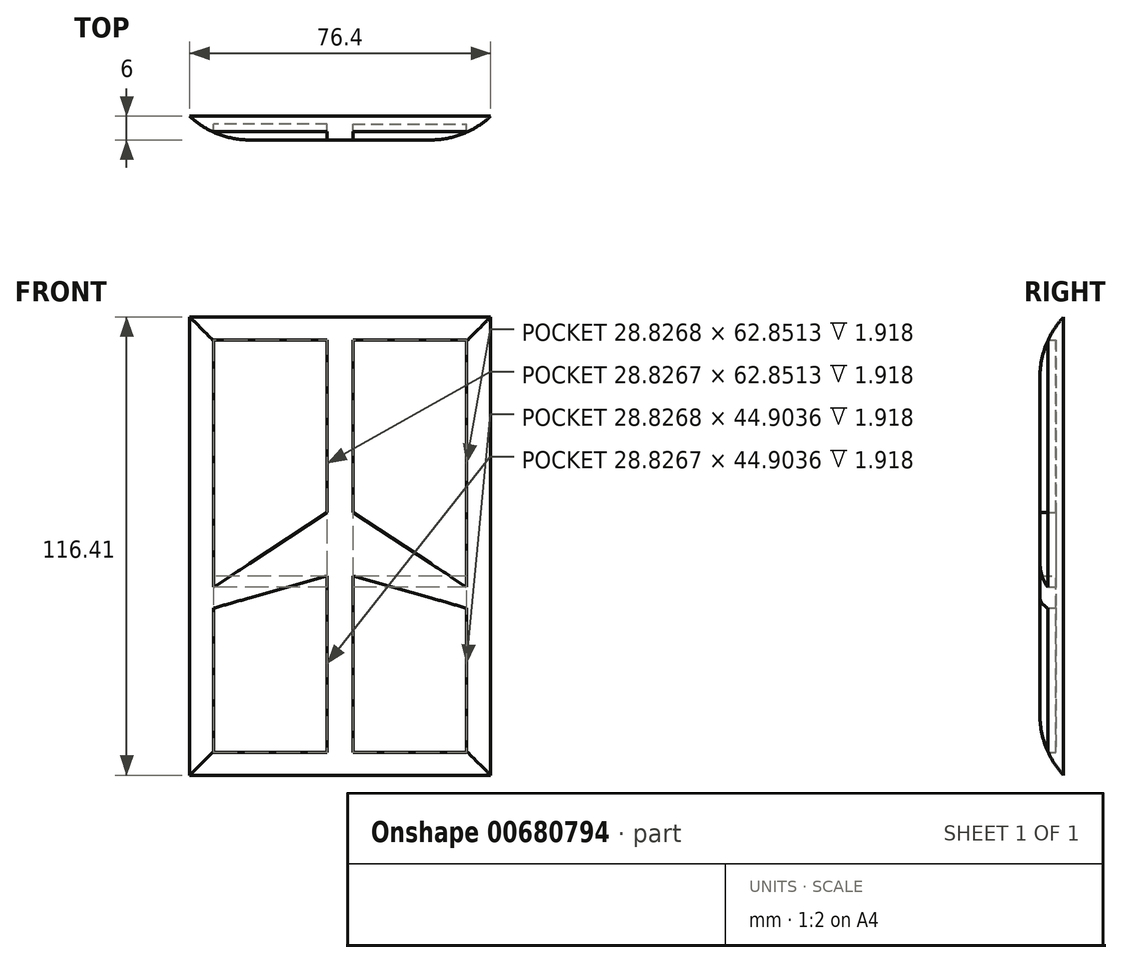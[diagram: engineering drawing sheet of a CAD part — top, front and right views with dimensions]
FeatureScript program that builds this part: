
annotation { "Feature Type Name" : "Feature", "Feature Type Description" : "" }
export const myFeature = defineFeature(function(context is Context, id is Id, definition is map)
    precondition{}
    {
        {
            var Q0;
            Q0=qCreatedBy(makeId("Front.planeOp"),FACE);
            var sketch = newSketch(context, id + "F0", { "sketchPlane" : qUnion([Q0])});
            skLineSegment(sketch, "E0.bottom", {"start": v(-19.82, 37.7) * mm, "end": v(44.44, 37.7) * mm});
            skLineSegment(sketch, "E0.top", {"start": v(-19.82, -67.16) * mm, "end": v(44.44, -67.16) * mm});
            skLineSegment(sketch, "E0.left", {"start": v(-19.82, 37.7) * mm, "end": v(-19.82, -67.16) * mm});
            skLineSegment(sketch, "E0.right", {"start": v(44.44, 37.7) * mm, "end": v(44.44, -67.16) * mm});
            skPoint(sketch, "E1", {"position": v(-25.9, -72.94) * mm});
            skPoint(sketch, "E2", {"position": v(50.51, -72.94) * mm});
            skPoint(sketch, "E3", {"position": v(50.51, 43.47) * mm});
            skPoint(sketch, "E4", {"position": v(-25.9, 43.47) * mm});
            skLineSegment(sketch, "E5", {"start": v(-25.9, -72.94) * mm, "end": v(50.51, -72.94) * mm});
            skLineSegment(sketch, "E6", {"start": v(-25.9, 43.47) * mm, "end": v(50.51, 43.47) * mm});
            skLineSegment(sketch, "E7", {"start": v(50.51, -72.94) * mm, "end": v(50.51, 43.47) * mm});
            skLineSegment(sketch, "E8", {"start": v(-25.9, -72.94) * mm, "end": v(-25.9, 43.47) * mm});
            skPoint(sketch, "E9", {"position": v(12.31, -67.16) * mm});
            skPoint(sketch, "E10", {"position": v(15.61, -67.16) * mm});
            skPoint(sketch, "E11", {"position": v(9, -67.16) * mm});
            skPoint(sketch, "E12", {"position": v(9, -6.18) * mm});
            skPoint(sketch, "E13", {"position": v(15.61, -6.18) * mm});
            skLineSegment(sketch, "E14", {"start": v(9, -6.18) * mm, "end": v(-19.82, -25.16) * mm});
            skLineSegment(sketch, "E15", {"start": v(9, -67.16) * mm, "end": v(9, -22.26) * mm});
            skLineSegment(sketch, "E16", {"start": v(15.61, -67.16) * mm, "end": v(15.61, -22.26) * mm});
            skLineSegment(sketch, "E17", {"start": v(9, -22.26) * mm, "end": v(-19.82, -30.5) * mm});
            skPoint(sketch, "E18", {"position": v(44.44, -30.5) * mm});
            skPoint(sketch, "E19", {"position": v(44.44, -25.16) * mm});
            skLineSegment(sketch, "E20", {"start": v(15.61, -6.18) * mm, "end": v(44.44, -25.16) * mm});
            skLineSegment(sketch, "E21", {"start": v(15.61, -22.26) * mm, "end": v(44.44, -30.5) * mm});
            skPoint(sketch, "E22", {"position": v(15.61, 37.7) * mm});
            skPoint(sketch, "E23", {"position": v(9, 37.7) * mm});
            skLineSegment(sketch, "E24", {"start": v(15.61, -6.18) * mm, "end": v(15.61, 37.7) * mm});
            skLineSegment(sketch, "E25", {"start": v(9, -6.18) * mm, "end": v(9, 37.7) * mm});
            skSolve(sketch);
        }
        {
            var Q0;
            {var subQ3=sQuery(id+"F0.wireOp",EDGE,"E14");Q0=makeQuery(id+"F0.imprint","IMPRINT",FACE,{"disambiguationData":[TD([[makeQuery(id+"F0.imprint","IMPRINT",EDGE,{"derivedFrom":subQ3}),1.0]])]});}
            extrude(context, id + "F1", {"entities" : qUnion([Q0]), "depth" : 6 * mm, "offsetDistance" : 25.4 * mm});
        }
        {
            var Q0;
            Q0=makeQuery(id+"F0.imprint","IMPRINT",FACE,{"disambiguationData":[TD([[makeQuery(id+"F0.imprint","IMPRINT",EDGE,{"derivedFrom":sQuery(id+"F0.wireOp",EDGE,"E5")}),1.0]])]});
            extrude(context, id + "F2", {"entities" : qUnion([Q0]), "operationType" : NewBodyOperationType.ADD, "depth" : 6 * mm, "offsetDistance" : 25.4 * mm});
        }
        {
            var Q0;
            {var subQ4=sQuery(id+"F0.wireOp",EDGE,"E14");Q0=makeQuery(id+"F0.imprint","IMPRINT",FACE,{"disambiguationData":[TD([[makeQuery(id+"F0.imprint","IMPRINT",EDGE,{"derivedFrom":subQ4}),-1.0]])]});}
            var Q1;
            {var subQ3=sQuery(id+"F0.wireOp",EDGE,"PBUEc8fT-vQCt-3he3-9Wfb-PLxy9nkW7Vk9");Q1=makeQuery(id+"F0.imprint","IMPRINT",FACE,{"disambiguationData":[TD([[makeQuery(id+"F0.imprint","IMPRINT",EDGE,{"derivedFrom":subQ3}),-1.0]])]});}
            var Q2;
            {var subQ3=sQuery(id+"F0.wireOp",EDGE,"E16");Q2=makeQuery(id+"F0.imprint","IMPRINT",FACE,{"disambiguationData":[TD([[makeQuery(id+"F0.imprint","IMPRINT",EDGE,{"derivedFrom":subQ3}),-1.0]])]});}
            var Q3;
            {var subQ3=sQuery(id+"F0.wireOp",EDGE,"E15");Q3=makeQuery(id+"F0.imprint","IMPRINT",FACE,{"disambiguationData":[TD([[makeQuery(id+"F0.imprint","IMPRINT",EDGE,{"derivedFrom":subQ3}),1.0]])]});}
            var Q4;
            {var subQ4=sQuery(id+"F0.wireOp",EDGE,"E20");Q4=makeQuery(id+"F0.imprint","IMPRINT",FACE,{"disambiguationData":[TD([[makeQuery(id+"F0.imprint","IMPRINT",EDGE,{"derivedFrom":subQ4}),1.0]])]});}
            extrude(context, id + "F3", {"entities" : qUnion([Q0, Q1, Q2, Q3, Q4]), "operationType" : NewBodyOperationType.ADD, "depth" : 2 * mm, "offsetDistance" : 25.4 * mm});
        }
        {
            var Q0;
            Q0=makeQuery(id+"F2.opExtrude","CAP_EDGE",EDGE,{"disambiguationData":[OSD([sQuery(id+"F0.wireOp",EDGE,"E8")])],"isStart":false});
            var Q1;
            Q1=makeQuery(id+"F2.opExtrude","CAP_EDGE",EDGE,{"disambiguationData":[OSD([sQuery(id+"F0.wireOp",EDGE,"E5")])],"isStart":false});
            var Q2;
            Q2=makeQuery(id+"F2.opExtrude","CAP_EDGE",EDGE,{"disambiguationData":[OSD([sQuery(id+"F0.wireOp",EDGE,"E7")])],"isStart":false});
            var Q3;
            Q3=makeQuery(id+"F2.opExtrude","CAP_EDGE",EDGE,{"disambiguationData":[OSD([sQuery(id+"F0.wireOp",EDGE,"E6")])],"isStart":false});
            fillet(context, id + "F4", {"entities" : qUnion([Q0, Q1, Q2, Q3]), "radius" : 22.1 * mm, "allowEdgeOverflow" : false});
        }
    });
